FCSTD DOCUMENT  (FreeCAD 1.0RUnknown)
Label: assambly-control-assembly
License: All rights reserved
LicenseURL: https://en.wikipedia.org/wiki/All_rights_reserved
objects: App::FeaturePython×4, App::Link×3, Assembly::AssemblyObject×1, Assembly::JointGroup×1
EXTERNAL_REF file=assambly-control-varset.FCStd obj=Sketch
EXTERNAL_REF file=assambly-control-varset.FCStd obj=Body

FEATURE [App::Link] SkeletonSketch
  LinkPlacement = pos=(961.104,1249.18,-673.697) rot=(1,0,0;1.5708rad)
  LinkedObject = -> <external assambly-control-varset.FCStd>#Sketch
  Placement = pos=(961.104,1249.18,-673.697) rot=(1,0,0;1.5708rad)
FEATURE [App::Link] SideBody
  LinkPlacement = pos=(1461.1,749.176,-673.697) rot=(0.996164,0,0;0rad)
  LinkedObject = -> <external assambly-control-varset.FCStd>#Body
  Placement = pos=(1461.1,749.176,-673.697) rot=(0.996164,0,0;0rad)
FEATURE [App::Link] SideBody001
  LinkPlacement = pos=(431.104,749.176,-673.697) rot=(0.99808,0,0;0rad)
  LinkedObject = -> <external assambly-control-varset.FCStd>#Body
  Placement = pos=(431.104,749.176,-673.697) rot=(0.99808,0,0;0rad)
FEATURE [App::FeaturePython] GroundedJoint001  # Assembly grounded joint (typed FeaturePython)
  ObjectToGround = -> SkeletonSketch
  Placement = pos=(961.104,1249.18,-673.697) rot=(1,0,0;1.5708rad)
FEATURE [App::FeaturePython] Joint  label="Fixed"  # Assembly joint (typed FeaturePython)
  Activated = true
  AngleMax = 0
  AngleMin = 0
  Detach1 = false
  Detach2 = false
  Distance = 0
  Distance2 = 0
  EnableAngleMax = false
  EnableAngleMin = false
  EnableLengthMax = false
  EnableLengthMin = false
  JointType = 0 (Fixed)
  LengthMax = 0
  LengthMin = 0
  Offset1 = pos=(0,0,0) rot=(-1,0,0;1.5708rad)
  Placement1 = pos=(30,500,2500) rot=(-1,0,0;1.5708rad)
  Placement2 = pos=(-500,2500,-2.274e-13) rot=(0,0,1;0rad)
  Reference1 = -> Assembly [SideBody001.Vertex6,SideBody001.Vertex6]
  Reference2 = -> Assembly [SkeletonSketch.Vertex4,SkeletonSketch.Vertex4]
FEATURE [App::FeaturePython] Joint001  label="Fixed001"  # Assembly joint (typed FeaturePython)
  Activated = true
  AngleMax = 0
  AngleMin = 0
  Detach1 = false
  Detach2 = false
  Distance = 0
  Distance2 = 0
  EnableAngleMax = false
  EnableAngleMin = false
  EnableLengthMax = false
  EnableLengthMin = false
  JointType = 0 (Fixed)
  LengthMax = 0
  LengthMin = 0
  Offset1 = pos=(0,0,0) rot=(0.57735,0.57735,-0.57735;2.0944rad)
  Placement1 = pos=(500,2500,0) rot=(-1,0,0;1.5708rad)
  Placement2 = pos=(0,500,2500) rot=(0,0,1;0rad)
  Reference1 = -> Assembly [SkeletonSketch.Edge3,SkeletonSketch.Vertex3]
  Reference2 = -> Assembly [SideBody.Vertex5,SideBody.Vertex5]
FEATURE [Assembly::AssemblyObject] Assembly
  Group = -> [Joints,SkeletonSketch,SideBody,SideBody001,GroundedJoint,GroundedJoint001,Joint,Joint001]
  Origin = -> Origin
  Type = Assembly
FEATURE [Assembly::JointGroup] Joints
  Group = -> [GroundedJoint,GroundedJoint001,Joint,Joint001]
FEATURE [App::FeaturePython] GroundedJoint  # Assembly grounded joint (typed FeaturePython)
  ObjectToGround = -> Joints

RESOLVED EXTERNAL PARTS (link-assembly join: the EXTERNAL_REF files above that resolve inside this repo's crawl, each included once):
---- part assambly-control-varset.FCStd = doc fcstd_f15b0effd19f ----
FCSTD DOCUMENT  (FreeCAD 1.0RUnknown)
Label: assambly-control-varset
License: All rights reserved
LicenseURL: https://en.wikipedia.org/wiki/All_rights_reserved
objects: Sketcher::SketchObject×3, PartDesign::Pad×2, PartDesign::Body×2, App::VarSet×1
note: 14 computed .brp shape members not serialized (recipe doc carries the construction recipe); baked Part::Feature solids carry a one-line shape summary decoded from their .brp

FEATURE [Sketcher::SketchObject] Sketch  label="SkeletonSketch"
  ArcFitTolerance = 1e-06
  FullyConstrained = true
  MakeInternals = false
  Placement = pos=(0,0,0) rot=(1,0,0;1.5708rad)
  expr: Constraints[20] = VarSet.Shelf3Haight
  expr: Constraints[21] = VarSet.Shelf2Height
  expr: Constraints[22] = VarSet.Shelf1Height
  expr: Constraints[7] = VarSet.CabWidth
  expr: Constraints[8] = VarSet.CabHeight
  sketch-geometry (7):
    g0: LineSegment StartX=-500 StartY=0 StartZ=0 EndX=500 EndY=0 EndZ=0
    g1: LineSegment StartX=500 StartY=0 StartZ=0 EndX=500 EndY=2500 EndZ=0
    g2: LineSegment StartX=500 StartY=2500 StartZ=0 EndX=-500 EndY=2500 EndZ=0
    g3: LineSegment StartX=-500 StartY=2500 StartZ=0 EndX=-500 EndY=0 EndZ=0
    g4: LineSegment StartX=-500 StartY=500 StartZ=0 EndX=500 EndY=500 EndZ=0
    g5: LineSegment StartX=-500 StartY=1000 StartZ=0 EndX=500 EndY=1000 EndZ=0
    g6: LineSegment StartX=-500 StartY=1500 StartZ=0 EndX=500 EndY=1500 EndZ=0
  constraints (23):
    c: Coincident(g0,g1)
    c: Coincident(g1,g2)
    c: Coincident(g2,g3)
    c: Coincident(g3,g0)
    c: Horizontal(g2)
    c: Vertical(g1)
    c: Vertical(g3)
    c: Distance(g1,g3) = 1000
    c: Distance(g0,g2) = 2500
    c: PointOnObject(g0,g-1)
    c: Symmetric(g0,g0,g-2)
    c: PointOnObject(g4,g3)
    c: PointOnObject(g4,g1)
    c: Horizontal(g4)
    c: PointOnObject(g5,g3)
    c: PointOnObject(g5,g1)
    c: Horizontal(g5)
    c: PointOnObject(g6,g3)
    c: PointOnObject(g6,g1)
    c: Horizontal(g6)
    c: DistanceY(g-1,g4) = 500
    c: DistanceY(g-1,g5) = 1000
    c: DistanceY(g-1,g6) = 1500
FEATURE [App::VarSet] VarSet
  CabHeight = 2580
  CabWidth = 1000
  Shelf1Height = 1500
  Shelf2Height = 1000
  Shelf3Haight = 500
FEATURE [Sketcher::SketchObject] Sketch001
  ArcFitTolerance = 1e-06
  AttachmentSupport = -> [YZ_Plane]
  FullyConstrained = true
  MakeInternals = false
  MapMode = 5
  Placement = pos=(0,0,0) rot=(0.57735,0.57735,0.57735;2.0944rad)
  expr: Constraints[8] = VarSet.CabWidth
  expr: Constraints[9] = VarSet.CabHeight
  sketch-geometry (4):
    g0: LineSegment StartX=-500 StartY=0 StartZ=0 EndX=500 EndY=0 EndZ=0
    g1: LineSegment StartX=500 StartY=0 StartZ=0 EndX=500 EndY=2500 EndZ=0
    g2: LineSegment StartX=500 StartY=2500 StartZ=0 EndX=-500 EndY=2500 EndZ=0
    g3: LineSegment StartX=-500 StartY=2500 StartZ=0 EndX=-500 EndY=0 EndZ=0
  constraints (11):
    c: Coincident(g0,g1)
    c: Coincident(g1,g2)
    c: Coincident(g2,g3)
    c: Coincident(g3,g0)
    c: Horizontal(g0)
    c: Horizontal(g2)
    c: Vertical(g1)
    c: Vertical(g3)
    c: Distance(g0,g0) = 1000
    c: DistanceY(g1,g1) = 2500
    c: Symmetric(g0,g0,g-1)
FEATURE [PartDesign::Pad] Pad
  Direction = (1,0,0)
  Length = 30
  Length2 = 10
  Placement = pos=(0,0,0) rot=(1,1,1;2.0944rad)
  Profile = -> Sketch001
  ReferenceAxis = -> Sketch001 [N_Axis]
  Refine = true
  Suppressed = false
  Type = 0
FEATURE [PartDesign::Body] Body  label="SideBody"
  AllowCompound = false
  Group = -> [Sketch001,Pad]
  Origin = -> Origin
  Tip = -> Pad
FEATURE [Sketcher::SketchObject] Sketch002
  ArcFitTolerance = 1e-06
  AttachmentSupport = -> [XY_Plane001]
  FullyConstrained = true
  MakeInternals = false
  MapMode = 5
  expr: Constraints[10] = VarSet.CabWidth
  sketch-geometry (5):
    g0: LineSegment StartX=500 StartY=-500 StartZ=0 EndX=500 EndY=500 EndZ=0
    g1: LineSegment StartX=500 StartY=500 StartZ=0 EndX=-500 EndY=500 EndZ=0
    g2: LineSegment StartX=-500 StartY=500 StartZ=0 EndX=-500 EndY=-500 EndZ=0
    g3: LineSegment StartX=-500 StartY=-500 StartZ=0 EndX=500 EndY=-500 EndZ=0
    g4: GeomPoint [constr] X=0 Y=0 Z=0
  constraints (12):
    c: Coincident(g0,g1)
    c: Coincident(g1,g2)
    c: Coincident(g2,g3)
    c: Coincident(g3,g0)
    c: Vertical(g0)
    c: Vertical(g2)
    c: Horizontal(g1)
    c: Horizontal(g3)
    c: Symmetric(g2,g0,g4)
    c: Coincident(g4,g-1)
    c: DistanceY(g2,g2) = 1000
    c: Equal(g2,g1)
FEATURE [PartDesign::Pad] Pad001
  Direction = (0,0,1)
  Length = 30
  Length2 = 10
  Profile = -> Sketch002
  ReferenceAxis = -> Sketch002 [N_Axis]
  Refine = true
  Suppressed = false
  Type = 0
FEATURE [PartDesign::Body] Body001  label="ShelfBody"
  AllowCompound = false
  Group = -> [Sketch002,Pad001]
  Origin = -> Origin001
  Tip = -> Pad001
